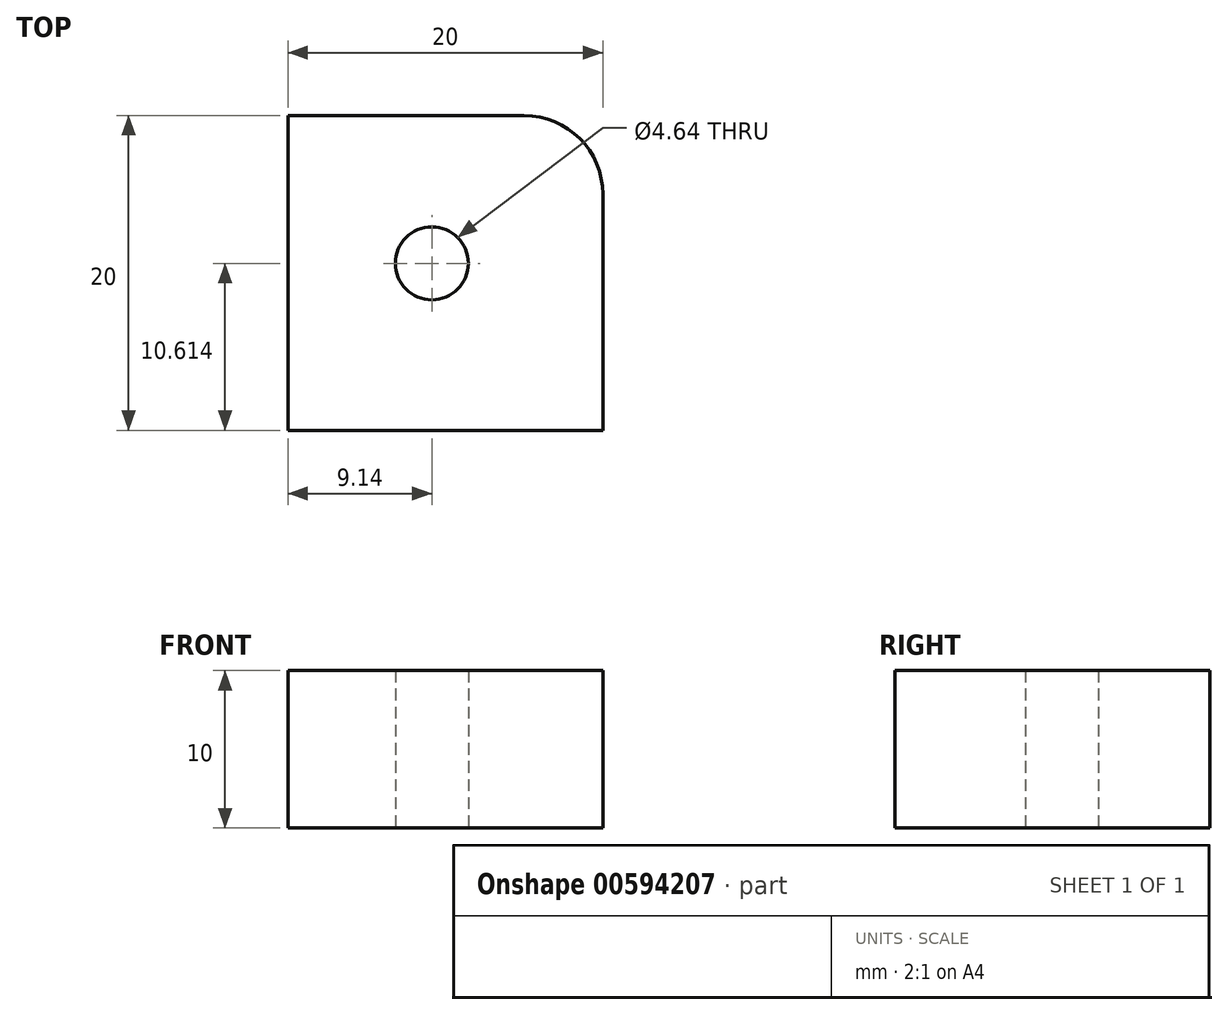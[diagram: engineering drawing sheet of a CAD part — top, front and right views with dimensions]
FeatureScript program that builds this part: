
annotation { "Feature Type Name" : "Feature", "Feature Type Description" : "" }
export const myFeature = defineFeature(function(context is Context, id is Id, definition is map)
    precondition{}
    {
        {
            var Q0;
            Q0=qCreatedBy(makeId("Top.planeOp"),FACE);
            var sketch = newSketch(context, id + "F0", { "sketchPlane" : qUnion([Q0])});
            skLineSegment(sketch, "E0.bottom", {"start": v(-9.14, 19.39) * mm, "end": v(5.86, 19.39) * mm});
            skLineSegment(sketch, "E0.top", {"start": v(-9.14, -0.61) * mm, "end": v(10.86, -0.61) * mm});
            skLineSegment(sketch, "E0.left", {"start": v(-9.14, 19.39) * mm, "end": v(-9.14, -0.61) * mm});
            skLineSegment(sketch, "E0.right", {"start": v(10.86, 14.39) * mm, "end": v(10.86, -0.61) * mm});
            skPoint(sketch, "E1.visualSharp", {"position": v(10.86, 19.39) * mm});
            skArc(sketch, "E1.filletArc", {"start": v(10.86, 14.39) * mm, "mid": v(9.4, 17.92) * mm, "end": v(5.86, 19.39) * mm});
            skCircle(sketch, "E2", {"center": v(0, 10) * mm, "radius": 2.32 * mm});
            skSolve(sketch);
        }
        {
            var Q0;
            Q0=makeQuery(id+"F0.imprint","IMPRINT",FACE,{"disambiguationData":[TD([[makeQuery(id+"F0.imprint","IMPRINT",EDGE,{"derivedFrom":sQuery(id+"F0.wireOp",EDGE,"E0.bottom")}),-1.0]])]});
            extrude(context, id + "F1", {"entities" : qUnion([Q0]), "depth" : 10 * mm, "offsetDistance" : 25 * mm});
        }
    });
